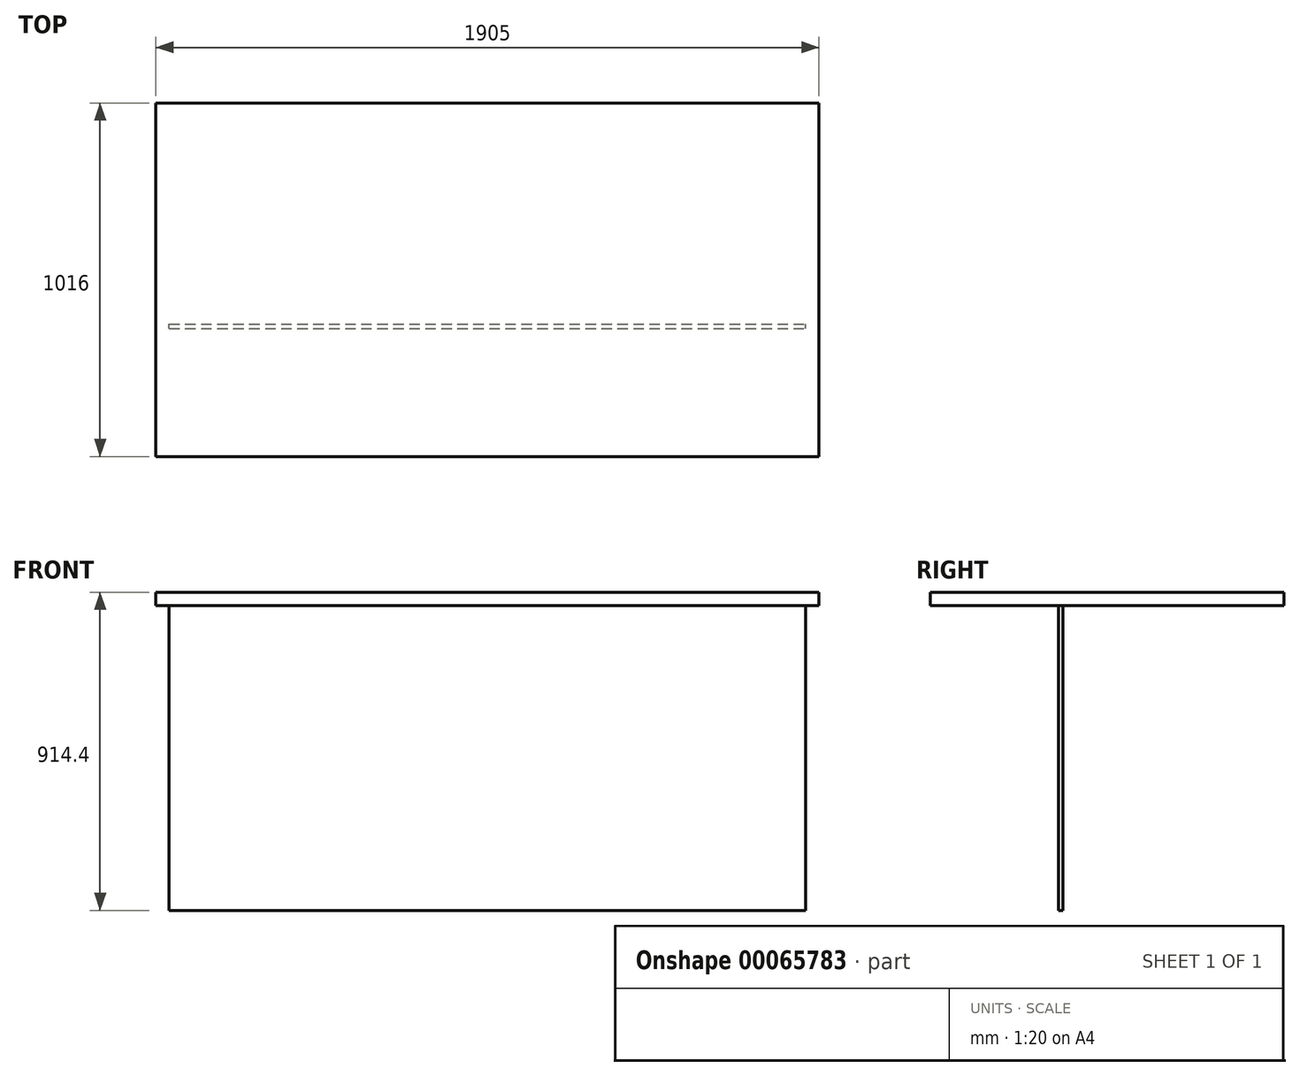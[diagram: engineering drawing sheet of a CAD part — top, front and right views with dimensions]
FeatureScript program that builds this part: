
annotation { "Feature Type Name" : "Feature", "Feature Type Description" : "" }
export const myFeature = defineFeature(function(context is Context, id is Id, definition is map)
    precondition{}
    {
        {
            var Q0;
            Q0=qCreatedBy(makeId("Top.planeOp"),FACE);
            var sketch = newSketch(context, id + "F0", { "sketchPlane" : qUnion([Q0])});
            skLineSegment(sketch, "E0.rect.bottom", {"start": v(914.4, 508) * mm, "end": v(-914.4, 508) * mm});
            skLineSegment(sketch, "E0.rect.top", {"start": v(914.4, -508) * mm, "end": v(-914.4, -508) * mm});
            skLineSegment(sketch, "E0.rect.left", {"start": v(914.4, 508) * mm, "end": v(914.4, -508) * mm});
            skLineSegment(sketch, "E0.rect.right", {"start": v(-914.4, 508) * mm, "end": v(-914.4, -508) * mm});
            skPoint(sketch, "E0.rect.middle", {"position": v(0, 0) * mm});
            skLineSegment(sketch, "E1.bottom", {"start": v(-914.4, 508) * mm, "end": v(-952.5, 508) * mm});
            skLineSegment(sketch, "E1.top", {"start": v(-914.4, -508) * mm, "end": v(-952.5, -508) * mm});
            skLineSegment(sketch, "E1.right", {"start": v(-952.5, 508) * mm, "end": v(-952.5, -508) * mm});
            skLineSegment(sketch, "E2.bottom", {"start": v(914.4, 508) * mm, "end": v(952.5, 508) * mm});
            skLineSegment(sketch, "E2.top", {"start": v(914.4, -508) * mm, "end": v(952.5, -508) * mm});
            skLineSegment(sketch, "E2.right", {"start": v(952.5, 508) * mm, "end": v(952.5, -508) * mm});
            skSolve(sketch);
        }
        {
            var Q0;
            Q0=makeQuery(id+"F0.imprint","IMPRINT",FACE,{"disambiguationData":[TD([[makeQuery(id+"F0.imprint","IMPRINT",EDGE,{"derivedFrom":sQuery(id+"F0.wireOp",EDGE,"E1.bottom")}),1.0]])]});
            var Q1;
            Q1=makeQuery(id+"F0.imprint","IMPRINT",FACE,{"disambiguationData":[TD([[makeQuery(id+"F0.imprint","IMPRINT",EDGE,{"derivedFrom":sQuery(id+"F0.wireOp",EDGE,"E0.rect.bottom")}),1.0]])]});
            var Q2;
            Q2=makeQuery(id+"F0.imprint","IMPRINT",FACE,{"disambiguationData":[TD([[makeQuery(id+"F0.imprint","IMPRINT",EDGE,{"derivedFrom":sQuery(id+"F0.wireOp",EDGE,"E2.bottom")}),-1.0]])]});
            extrude(context, id + "F1", {"entities" : qUnion([Q0, Q1, Q2]), "depth" : 38.1 * mm});
        }
        {
            var Q0;
            Q0=makeQuery(id+"F0.imprint","IMPRINT",FACE,{"disambiguationData":[TD([[makeQuery(id+"F0.imprint","IMPRINT",EDGE,{"derivedFrom":sQuery(id+"F0.wireOp",EDGE,"E1.bottom")}),1.0]])]});
            var Q1;
            Q1=makeQuery(id+"F0.imprint","IMPRINT",FACE,{"disambiguationData":[TD([[makeQuery(id+"F0.imprint","IMPRINT",EDGE,{"derivedFrom":sQuery(id+"F0.wireOp",EDGE,"E2.bottom")}),-1.0]])]});
            extrude(context, id + "F2", {"entities" : qUnion([Q0, Q1]), "operationType" : NewBodyOperationType.ADD, "oppositeDirection" : true, "depth" : 876.3 * mm});
        }
        {
            var Q0;
            {var subQ0=sQuery(id+"F0.wireOp",EDGE,"E2.top");var subQ1=sQuery(id+"F0.wireOp",EDGE,"E1.top");Q0=makeQuery(id+"F2.boolean.opBoolean","MERGE",FACE,{"derivedFrom":[makeQuery(id+"F1.opExtrude","SWEPT_FACE",FACE,{"disambiguationData":[OSD([sQuery(id+"F0.wireOp",EDGE,"E0.rect.top"),subQ1,subQ0])]}),makeQuery(id+"F2.opExtrude","SWEPT_FACE",FACE,{"disambiguationData":[OSD([subQ1])]}),makeQuery(id+"F2.opExtrude","SWEPT_FACE",FACE,{"disambiguationData":[OSD([subQ0])]})]});}
            cPlane(context, id + "F3", {"entities" : qUnion([Q0]), "cplaneType" : CPlaneType.OFFSET, "offset" : 381 * mm, "oppositeDirection" : true, "width" : 152.4 * mm, "height" : 152.4 * mm});
        }
        {
            var Q0;
            Q0=qCreatedBy(id+"F3.planeOp",FACE);
            var sketch = newSketch(context, id + "F4", { "sketchPlane" : qUnion([Q0])});
            skLineSegment(sketch, "E3.bottom", {"start": v(-914.4, 0) * mm, "end": v(914.4, 0) * mm});
            skLineSegment(sketch, "E3.top", {"start": v(-914.4, -876.3) * mm, "end": v(914.4, -876.3) * mm});
            skLineSegment(sketch, "E3.left", {"start": v(-914.4, 0) * mm, "end": v(-914.4, -876.3) * mm});
            skLineSegment(sketch, "E3.right", {"start": v(914.4, 0) * mm, "end": v(914.4, -876.3) * mm});
            skSolve(sketch);
        }
        {
            var Q0;
            Q0=qSketchRegion(id+"F4",true);
            extrude(context, id + "F5", {"entities" : qUnion([Q0]), "depth" : 12.7 * mm});
        }
        {
            var Q0;
            {var subQ0=sQuery(id+"F0.wireOp",EDGE,"E2.right");Q0=makeQuery(id+"F2.boolean.opBoolean","MERGE",FACE,{"derivedFrom":[makeQuery(id+"F1.opExtrude","SWEPT_FACE",FACE,{"disambiguationData":[OSD([subQ0])]}),makeQuery(id+"F2.opExtrude","SWEPT_FACE",FACE,{"disambiguationData":[OSD([subQ0])]})]});}
            var sketch = newSketch(context, id + "F6", { "sketchPlane" : qUnion([Q0])});
            skLineSegment(sketch, "E4.bottom", {"start": v(-508, -876.3) * mm, "end": v(508, -876.3) * mm});
            skLineSegment(sketch, "E4.top", {"start": v(-508, 0) * mm, "end": v(508, 0) * mm});
            skLineSegment(sketch, "E4.left", {"start": v(-508, -876.3) * mm, "end": v(-508, 0) * mm});
            skLineSegment(sketch, "E4.right", {"start": v(508, -876.3) * mm, "end": v(508, 0) * mm});
            skSolve(sketch);
        }
        {
            var Q0;
            Q0 = qSketchRegion(id + "F6", true);
            extrude(context, id + "F7", {"entities" : qUnion([Q0]), "operationType" : NewBodyOperationType.REMOVE, "oppositeDirection" : true, "depth" : 38.1 * mm});
        }
        {
            var Q0;
            {var subQ0=sQuery(id+"F0.wireOp",EDGE,"E1.right");Q0=makeQuery(id+"F2.boolean.opBoolean","MERGE",FACE,{"derivedFrom":[makeQuery(id+"F1.opExtrude","SWEPT_FACE",FACE,{"disambiguationData":[OSD([subQ0])]}),makeQuery(id+"F2.opExtrude","SWEPT_FACE",FACE,{"disambiguationData":[OSD([subQ0])]})]});}
            var sketch = newSketch(context, id + "F8", { "sketchPlane" : qUnion([Q0])});
            skLineSegment(sketch, "E5.bottom", {"start": v(-508, -876.3) * mm, "end": v(508, -876.3) * mm});
            skLineSegment(sketch, "E5.top", {"start": v(-508, 0) * mm, "end": v(508, 0) * mm});
            skLineSegment(sketch, "E5.left", {"start": v(-508, -876.3) * mm, "end": v(-508, 0) * mm});
            skLineSegment(sketch, "E5.right", {"start": v(508, -876.3) * mm, "end": v(508, 0) * mm});
            skSolve(sketch);
        }
        {
            var Q0;
            Q0 = qSketchRegion(id + "F8", true);
            extrude(context, id + "F9", {"entities" : qUnion([Q0]), "operationType" : NewBodyOperationType.REMOVE, "oppositeDirection" : true, "depth" : 38.1 * mm});
        }
    });
